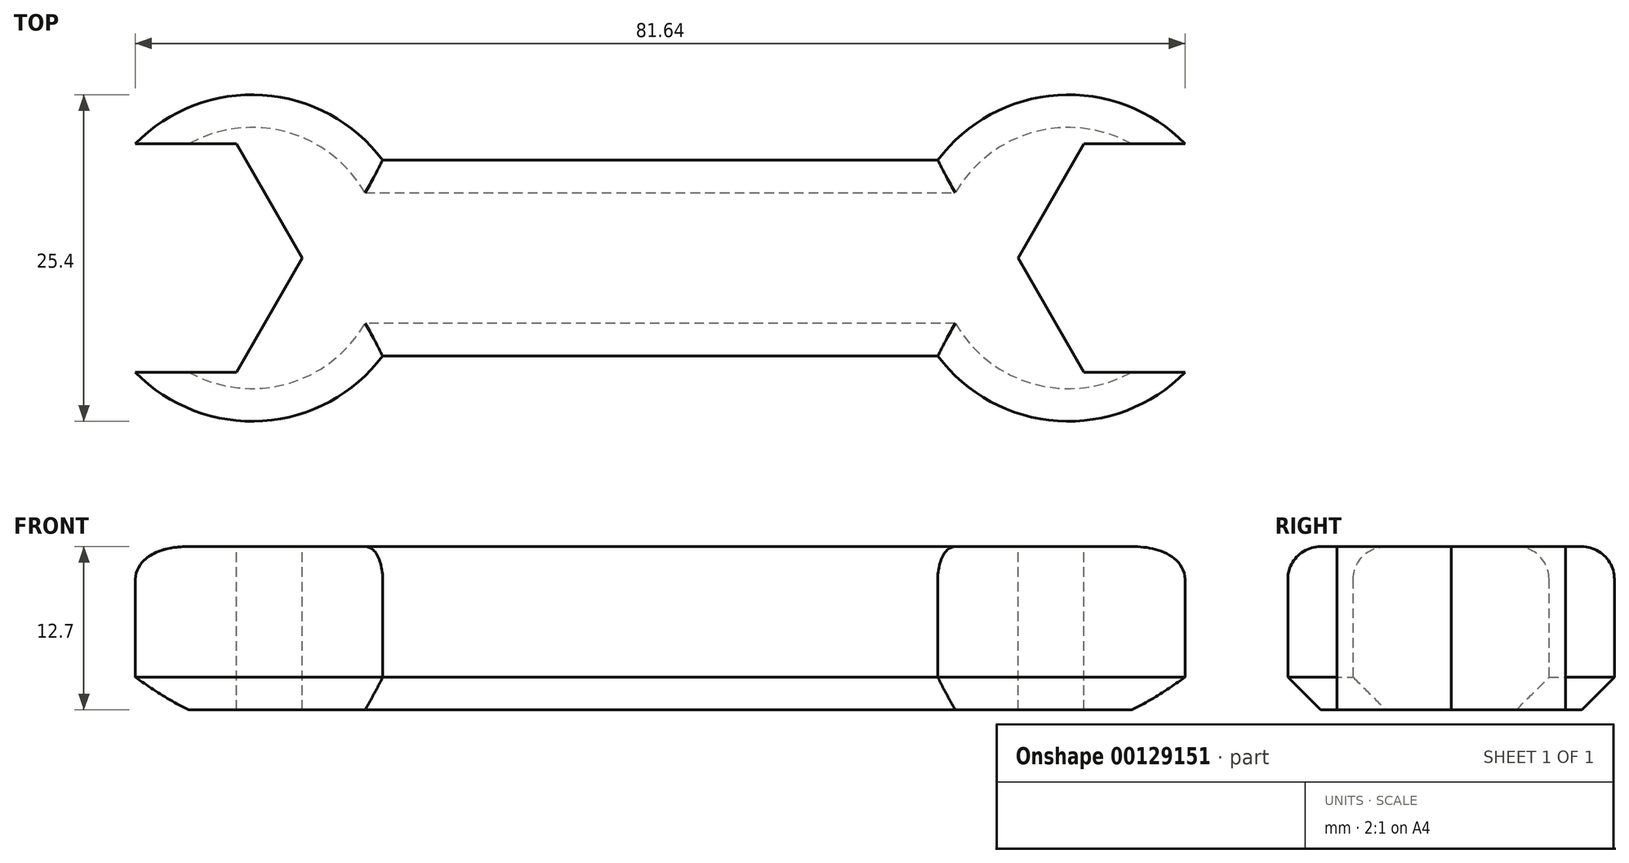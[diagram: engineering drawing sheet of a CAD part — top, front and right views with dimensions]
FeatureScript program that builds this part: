
annotation { "Feature Type Name" : "Feature", "Feature Type Description" : "" }
export const myFeature = defineFeature(function(context is Context, id is Id, definition is map)
    precondition{}
    {
        {
            var Q0;
            Q0=qCreatedBy(makeId("Top.planeOp"),FACE);
            var sketch = newSketch(context, id + "F0", { "sketchPlane" : qUnion([Q0])});
            skArc(sketch, "E0", {"start": v(-21.59, 7.62) * mm, "mid": v(-44.45, 0) * mm, "end": v(-21.59, -7.62) * mm});
            skArc(sketch, "E1", {"start": v(21.59, -7.62) * mm, "mid": v(44.45, 0) * mm, "end": v(21.59, 7.62) * mm});
            skLineSegment(sketch, "E2", {"start": v(-21.59, 7.62) * mm, "end": v(21.59, 7.62) * mm});
            skLineSegment(sketch, "E3", {"start": v(-21.59, -7.62) * mm, "end": v(21.59, -7.62) * mm});
            skLineSegment(sketch, "E4", {"start": v(-31.75, 0) * mm, "end": v(31.75, 0) * mm, "construction": true});
            skSolve(sketch);
        }
        {
            var Q0;
            Q0 = qSketchRegion(id + "F0", true);
            extrude(context, id + "F1", {"entities" : qUnion([Q0]), "endBound" : BoundingType.SYMMETRIC, "oppositeDirection" : true, "depth" : 12.7 * mm});
        }
        {
            var Q0;
            Q0=makeQuery(id+"F1.opExtrude","CAP_FACE",FACE,{"disambiguationData":[OSD([sQuery(id+"F0.wireOp",EDGE,"E0"),sQuery(id+"F0.wireOp",EDGE,"E1"),sQuery(id+"F0.wireOp",EDGE,"E2"),sQuery(id+"F0.wireOp",EDGE,"E3")])],"isStart":true});
            var sketch = newSketch(context, id + "F2", { "sketchPlane" : qUnion([Q0])});
            skCircle(sketch, "E5.cCircle", {"center": v(-38.1, 0) * mm, "radius": 8.9 * mm, "construction": true});
            skLineSegment(sketch, "E5.0", {"start": v(-43.23, -8.9) * mm, "end": v(-48.37, 0) * mm});
            skLineSegment(sketch, "E5.1", {"start": v(-48.37, 0) * mm, "end": v(-43.23, 8.9) * mm});
            skLineSegment(sketch, "E5.2", {"start": v(-43.23, 8.89) * mm, "end": v(-32.97, 8.89) * mm});
            skLineSegment(sketch, "E5.3", {"start": v(-32.97, 8.89) * mm, "end": v(-27.83, 0) * mm});
            skLineSegment(sketch, "E5.4", {"start": v(-27.83, 0) * mm, "end": v(-32.97, -8.9) * mm});
            skLineSegment(sketch, "E5.5", {"start": v(-32.97, -8.9) * mm, "end": v(-43.23, -8.9) * mm});
            skSolve(sketch);
        }
        {
            var Q0;
            Q0 = qSketchRegion(id + "F2", true);
            extrude(context, id + "F3", {"entities" : qUnion([Q0]), "endBound" : BoundingType.THROUGH_ALL, "oppositeDirection" : true, "depth" : 25.4 * mm});
        }
        {
            var Q0;
            Q0=makeQuery(id+"F3.opExtrude","SWEPT_BODY",BODY,{"disambiguationData":[OSD([sQuery(id+"F2.wireOp",EDGE,"E5.0"),sQuery(id+"F2.wireOp",EDGE,"E5.1"),sQuery(id+"F2.wireOp",EDGE,"E5.2"),sQuery(id+"F2.wireOp",EDGE,"E5.3"),sQuery(id+"F2.wireOp",EDGE,"E5.4"),sQuery(id+"F2.wireOp",EDGE,"E5.5")])]});
            var Q1;
            Q1=qCreatedBy(makeId("Right.planeOp"),FACE);
            mirror(context, id + "F4", {"operationType" : NewBodyOperationType.REMOVE, "entities" : qUnion([Q0]), "mirrorPlane" : qUnion([Q1])});
        }
        {
            var Q0;
            Q0=makeQuery(id+"F3.opExtrude","SWEPT_BODY",BODY,{"disambiguationData":[OSD([sQuery(id+"F2.wireOp",EDGE,"E5.0"),sQuery(id+"F2.wireOp",EDGE,"E5.1"),sQuery(id+"F2.wireOp",EDGE,"E5.2"),sQuery(id+"F2.wireOp",EDGE,"E5.3"),sQuery(id+"F2.wireOp",EDGE,"E5.4"),sQuery(id+"F2.wireOp",EDGE,"E5.5")])]});
            var Q1;
            Q1=makeQuery(id+"F1.opExtrude","SWEPT_BODY",BODY,{"disambiguationData":[OSD([sQuery(id+"F0.wireOp",EDGE,"E0"),sQuery(id+"F0.wireOp",EDGE,"E1"),sQuery(id+"F0.wireOp",EDGE,"E2"),sQuery(id+"F0.wireOp",EDGE,"E3")])]});
            booleanBodies(context, id + "F5", {"operationType" : BooleanOperationType.SUBTRACTION, "tools" : qUnion([Q0]), "targets" : qUnion([Q1])});
        }
        {
            var Q0;
            Q0=makeQuery(id+"F1.opExtrude","CAP_EDGE",EDGE,{"disambiguationData":[OSD([sQuery(id+"F0.wireOp",EDGE,"E3")])],"isStart":true});
            var Q1;
            {var subQ0=sQuery(id+"F0.wireOp",EDGE,"E0");var subQ1=sQuery(id+"F0.wireOp",EDGE,"E3");Q1=makeQuery(id+"F5.opBoolean","SPLIT",EDGE,{"disambiguationData":[TD([makeQuery(id+"F1.opExtrude","SWEPT_FACE",FACE,{"disambiguationData":[OSD([subQ1])]})])],"derivedFrom":makeQuery(id+"F1.opExtrude","CAP_EDGE",EDGE,{"disambiguationData":[OSD([subQ0])],"isStart":true})});}
            var Q2;
            {var subQ0=sQuery(id+"F0.wireOp",EDGE,"E0");var subQ1=sQuery(id+"F0.wireOp",EDGE,"E2");Q2=makeQuery(id+"F5.opBoolean","SPLIT",EDGE,{"disambiguationData":[TD([makeQuery(id+"F1.opExtrude","SWEPT_FACE",FACE,{"disambiguationData":[OSD([subQ1])]})])],"derivedFrom":makeQuery(id+"F1.opExtrude","CAP_EDGE",EDGE,{"disambiguationData":[OSD([subQ0])],"isStart":true})});}
            var Q3;
            Q3=makeQuery(id+"F1.opExtrude","CAP_EDGE",EDGE,{"disambiguationData":[OSD([sQuery(id+"F0.wireOp",EDGE,"E2")])],"isStart":true});
            var Q4;
            {var subQ0=sQuery(id+"F0.wireOp",EDGE,"E2");var subQ1=sQuery(id+"F0.wireOp",EDGE,"E1");Q4=makeQuery(id+"F4.boolean.opBoolean","SPLIT",EDGE,{"disambiguationData":[TD([makeQuery(id+"F1.opExtrude","SWEPT_FACE",FACE,{"disambiguationData":[OSD([subQ0])]})])],"derivedFrom":makeQuery(id+"F1.opExtrude","CAP_EDGE",EDGE,{"disambiguationData":[OSD([subQ1])],"isStart":true})});}
            var Q5;
            {var subQ0=sQuery(id+"F0.wireOp",EDGE,"E3");var subQ1=sQuery(id+"F0.wireOp",EDGE,"E1");Q5=makeQuery(id+"F4.boolean.opBoolean","SPLIT",EDGE,{"disambiguationData":[TD([makeQuery(id+"F1.opExtrude","SWEPT_FACE",FACE,{"disambiguationData":[OSD([subQ0])]})])],"derivedFrom":makeQuery(id+"F1.opExtrude","CAP_EDGE",EDGE,{"disambiguationData":[OSD([subQ1])],"isStart":true})});}
            fillet(context, id + "F6", {"entities" : qUnion([Q0, Q1, Q2, Q3, Q4, Q5]), "radius" : 2.54 * mm, "tangentPropagation" : true, "allowEdgeOverflow" : false});
        }
        {
            var Q0;
            {var subQ0=sQuery(id+"F0.wireOp",EDGE,"E0");var subQ1=sQuery(id+"F0.wireOp",EDGE,"E3");Q0=makeQuery(id+"F5.opBoolean","SPLIT",EDGE,{"disambiguationData":[TD([makeQuery(id+"F1.opExtrude","SWEPT_FACE",FACE,{"disambiguationData":[OSD([subQ1])]})])],"derivedFrom":makeQuery(id+"F1.opExtrude","CAP_EDGE",EDGE,{"disambiguationData":[OSD([subQ0])],"isStart":false})});}
            var Q1;
            Q1=makeQuery(id+"F1.opExtrude","CAP_EDGE",EDGE,{"disambiguationData":[OSD([sQuery(id+"F0.wireOp",EDGE,"E3")])],"isStart":false});
            var Q2;
            {var subQ0=sQuery(id+"F0.wireOp",EDGE,"E3");var subQ1=sQuery(id+"F0.wireOp",EDGE,"E1");Q2=makeQuery(id+"F4.boolean.opBoolean","SPLIT",EDGE,{"disambiguationData":[TD([makeQuery(id+"F1.opExtrude","SWEPT_FACE",FACE,{"disambiguationData":[OSD([subQ0])]})])],"derivedFrom":makeQuery(id+"F1.opExtrude","CAP_EDGE",EDGE,{"disambiguationData":[OSD([subQ1])],"isStart":false})});}
            var Q3;
            {var subQ0=sQuery(id+"F0.wireOp",EDGE,"E0");var subQ1=sQuery(id+"F0.wireOp",EDGE,"E2");Q3=makeQuery(id+"F5.opBoolean","SPLIT",EDGE,{"disambiguationData":[TD([makeQuery(id+"F1.opExtrude","SWEPT_FACE",FACE,{"disambiguationData":[OSD([subQ1])]})])],"derivedFrom":makeQuery(id+"F1.opExtrude","CAP_EDGE",EDGE,{"disambiguationData":[OSD([subQ0])],"isStart":false})});}
            var Q4;
            Q4=makeQuery(id+"F1.opExtrude","CAP_EDGE",EDGE,{"disambiguationData":[OSD([sQuery(id+"F0.wireOp",EDGE,"E2")])],"isStart":false});
            var Q5;
            {var subQ0=sQuery(id+"F0.wireOp",EDGE,"E2");var subQ1=sQuery(id+"F0.wireOp",EDGE,"E1");Q5=makeQuery(id+"F4.boolean.opBoolean","SPLIT",EDGE,{"disambiguationData":[TD([makeQuery(id+"F1.opExtrude","SWEPT_FACE",FACE,{"disambiguationData":[OSD([subQ0])]})])],"derivedFrom":makeQuery(id+"F1.opExtrude","CAP_EDGE",EDGE,{"disambiguationData":[OSD([subQ1])],"isStart":false})});}
            chamfer(context, id + "F7", {"entities" : qUnion([Q0, Q1, Q2, Q3, Q4, Q5]), "width" : 2.54 * mm, "tangentPropagation" : true});
        }
    });
